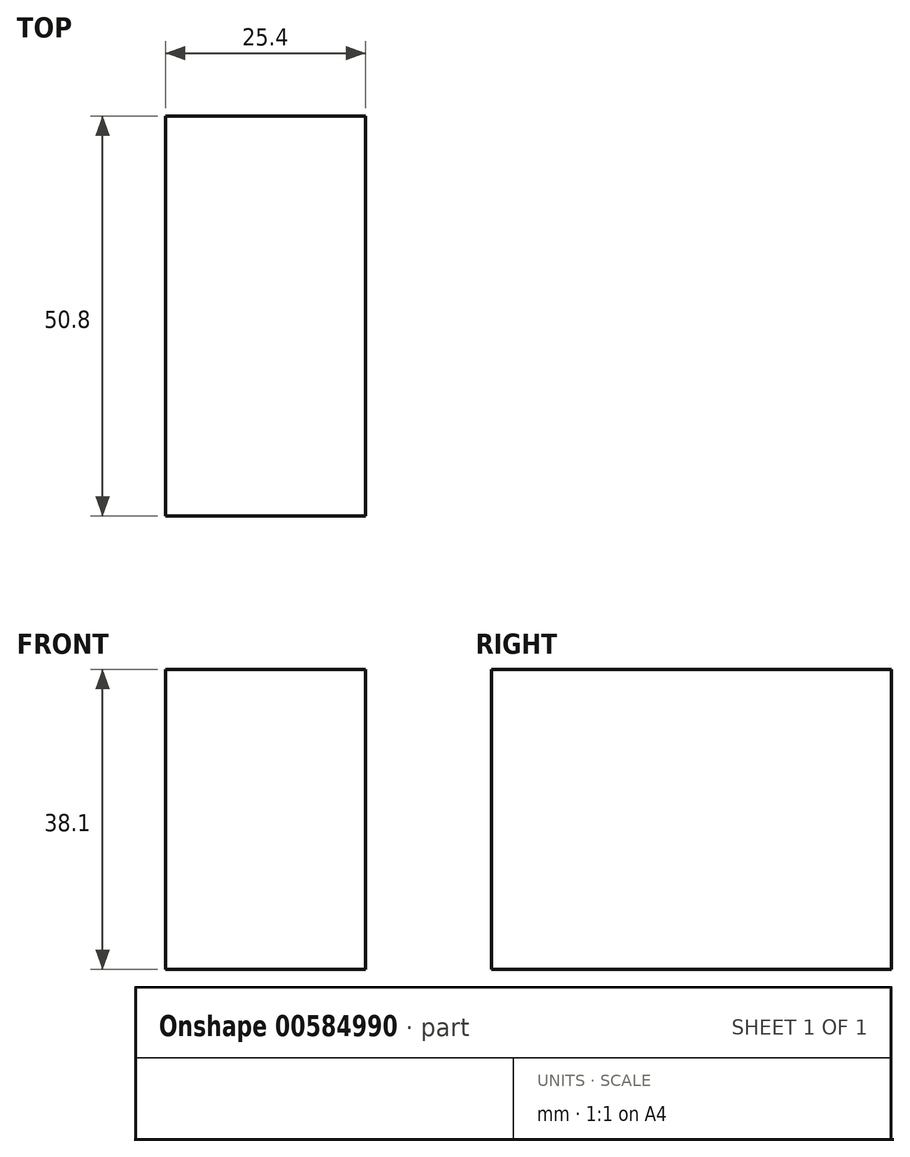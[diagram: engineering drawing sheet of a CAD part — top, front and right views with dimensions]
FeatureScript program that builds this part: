
annotation { "Feature Type Name" : "Feature", "Feature Type Description" : "" }
export const myFeature = defineFeature(function(context is Context, id is Id, definition is map)
    precondition{}
    {
        {
            var Q0;
            Q0=qCreatedBy(makeId("Top.planeOp"),FACE);
            var sketch = newSketch(context, id + "F0", { "sketchPlane" : qUnion([Q0])});
            skLineSegment(sketch, "E0.bottom", {"start": v(12.7, 25.4) * mm, "end": v(-12.7, 25.4) * mm});
            skLineSegment(sketch, "E0.top", {"start": v(12.7, -25.4) * mm, "end": v(-12.7, -25.4) * mm});
            skLineSegment(sketch, "E0.left", {"start": v(12.7, 25.4) * mm, "end": v(12.7, -25.4) * mm});
            skLineSegment(sketch, "E0.right", {"start": v(-12.7, 25.4) * mm, "end": v(-12.7, -25.4) * mm});
            skPoint(sketch, "E0.middle", {"position": v(0, 0) * mm});
            skSolve(sketch);
        }
        {
            var Q0;
            Q0 = qSketchRegion(id + "F0", true);
            extrude(context, id + "F1", {"entities" : qUnion([Q0]), "depth" : 38.1 * mm, "offsetDistance" : 25.4 * mm});
        }
    });
